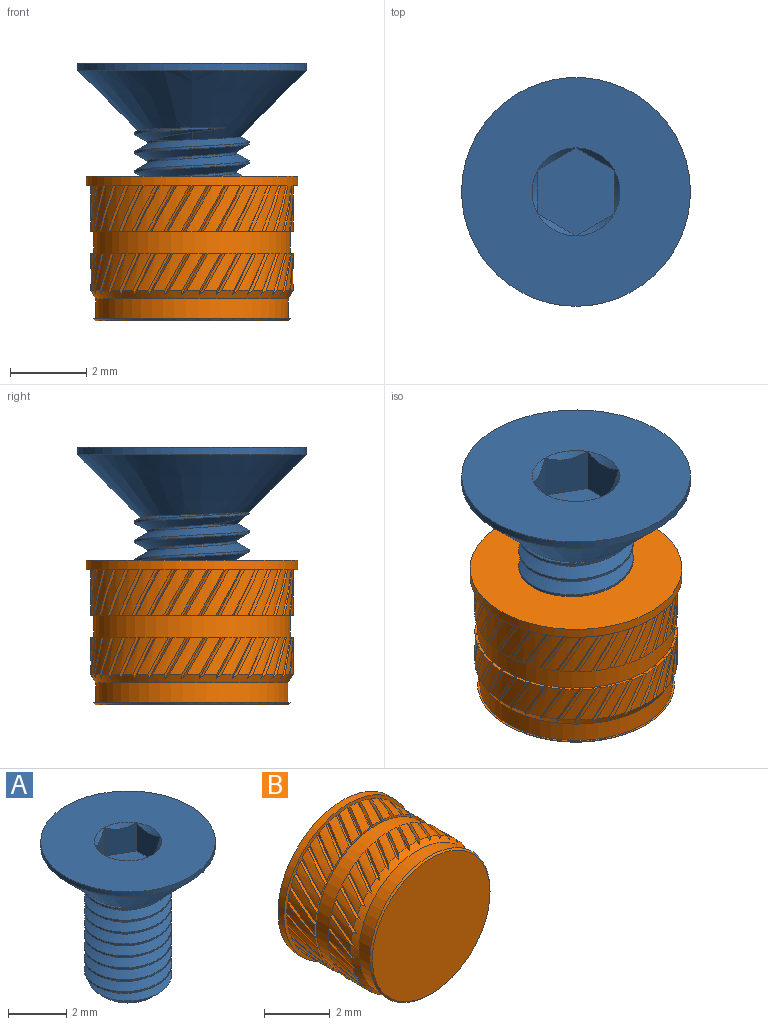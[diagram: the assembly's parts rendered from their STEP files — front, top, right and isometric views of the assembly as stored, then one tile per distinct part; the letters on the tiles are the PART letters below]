
ASSEMBLY  parts=2 mates=1
PART A: 23 faces, bbox 6.4x6.4x6.6 mm
  f0: cone r=1.15mm half-angle=45deg, axis (0,0,1), area 0.1mm2, adj f10,f17
  f1: cone r=1.5mm half-angle=45deg, axis (0,0,1), area 31.8mm2, adj f2,f3,f6,f7,f8
  f2: cone r=1.5mm half-angle=45deg, axis (0,0,1), area 0.2mm2, adj f1,f5,f7,f8
  f3: cylinder r=3mm len=6mm, axis (0,0,1), area 3.8mm2, adj f1,f10
  f4: cone r=1.12mm half-angle=45deg, axis (0,0,1), area 2.4mm2, adj f5,f6,f7,f8,f9
  f5: cylinder r=1.18mm len=3.93mm, axis (0,0,1), area 3.6mm2, adj f2,f4,f7,f8
  f6: cylinder r=1.5mm len=3.93mm, axis (0,0,-1), area 4.6mm2, adj f1,f4,f7,f8
  f7: bspline ~4.69x3.46mm, area 24.8mm2, adj f1,f2,f4,f5,f6
  f8: bspline ~4.35x3.46mm, area 24.8mm2, adj f1,f2,f4,f5,f6
  f9: plane 2.25x2.25mm, normal (0,0,-1), area 4mm2, adj f4
  f10: plane 6x6mm, normal (0,0,1), area 24.1mm2, adj f0,f3,f11,f12,f13,f14,f15
  f11: cone r=1.15mm half-angle=45deg, axis (0,0,1), area 0mm2, adj f10,f18
  f12: cone r=1.15mm half-angle=45deg, axis (0,0,1), area 0mm2, adj f10,f19
  f13: cone r=1.15mm half-angle=45deg, axis (0,0,1), area 0mm2, adj f10,f20
  f14: cone r=1.15mm half-angle=45deg, axis (0,0,1), area 0mm2, adj f10,f21
  f15: cone r=1.15mm half-angle=45deg, axis (0,0,1), area 0mm2, adj f10,f22
  f16: plane 2.31x2mm, normal (0,0,1), area 3.5mm2, adj f17,f18,f19,f20,f21,f22
  f17: plane 1.3x1.27mm, normal (-1,0,0), area 1.3mm2, adj f0,f16,f18,f22
  f18: plane 1.63x1.44mm, normal (-0.5,-0.87,0), area 1.3mm2, adj f11,f16,f17,f19
  f19: plane 1.63x1.44mm, normal (0.5,-0.87,0), area 1.3mm2, adj f12,f16,f18,f20
  f20: plane 1.63x1.59mm, normal (1,0,0), area 1.3mm2, adj f13,f16,f19,f21
  f21: plane 1.63x1.44mm, normal (0.5,0.87,0), area 1.3mm2, adj f14,f16,f20,f22
  f22: plane 1.63x1.44mm, normal (-0.5,0.87,0), area 1.3mm2, adj f15,f16,f17,f21
PART B: 227 faces, bbox 5.6x3.8x5.6 mm
  f0: cylinder r=2.58mm len=5.16mm, axis (0,1,0), area 9.3mm2, adj f225,f226
  f1: cone r=2.58mm half-angle=45deg, axis (0,1,0), area 1.2mm2, adj f151,f152
  f2: cone r=2.65mm half-angle=30deg, axis (0,1,0), area 3.9mm2, adj f5,f7,f8,f9,f10,f11,f12,f13
  f3: cylinder r=2.78mm len=5.56mm, axis (0,1,0), area 4.4mm2, adj f149,f150
  f4: cylinder r=2.65mm len=1.2mm, axis (0,1,0), area 0.4mm2, adj f149,f153,f156,f226
  f5: cylinder r=2.52mm len=5.05mm, axis (0,1,0), area 8.3mm2, adj f2,f151
  f6: cylinder r=2.65mm len=1.2mm, axis (0,1,0), area 0.4mm2, adj f149,f155,f158,f226
  f7: cylinder r=2.65mm len=0.97mm, axis (0,1,0), area 0.3mm2, adj f2,f47,f50,f225
  f8: cylinder r=2.65mm len=0.97mm, axis (0,1,0), area 0.3mm2, adj f2,f49,f51,f225
  f9: cylinder r=2.65mm len=0.97mm, axis (0,1,0), area 0.3mm2, adj f2,f111,f113,f225
  f10: cylinder r=2.65mm len=0.97mm, axis (0,1,0), area 0.3mm2, adj f2,f44,f114,f225
  f11: cylinder r=2.65mm len=0.97mm, axis (0,1,0), area 0.3mm2, adj f2,f109,f112,f225
  f12: cylinder r=2.65mm len=0.97mm, axis (0,1,0), area 0.3mm2, adj f2,f108,f110,f225
  f13: cylinder r=2.65mm len=0.97mm, axis (0,1,0), area 0.3mm2, adj f2,f103,f105,f225
  f14: cylinder r=2.65mm len=0.97mm, axis (0,1,0), area 0.3mm2, adj f2,f106,f107,f225
  f15: cylinder r=2.65mm len=0.97mm, axis (0,1,0), area 0.3mm2, adj f2,f101,f104,f225
  f16: cylinder r=2.65mm len=0.97mm, axis (0,1,0), area 0.3mm2, adj f2,f99,f102,f225
  f17: cylinder r=2.65mm len=0.97mm, axis (0,1,0), area 0.3mm2, adj f2,f97,f100,f225
  f18: cylinder r=2.65mm len=0.97mm, axis (0,1,0), area 0.3mm2, adj f2,f93,f95,f225
  f19: cylinder r=2.65mm len=0.97mm, axis (0,1,0), area 0.3mm2, adj f2,f96,f98,f225
  f20: cylinder r=2.65mm len=0.97mm, axis (0,1,0), area 0.3mm2, adj f2,f91,f94,f225
  f21: cylinder r=2.65mm len=0.97mm, axis (0,1,0), area 0.3mm2, adj f2,f90,f92,f225
  f22: cylinder r=2.65mm len=0.97mm, axis (0,1,0), area 0.3mm2, adj f2,f88,f89,f225
  f23: cylinder r=2.65mm len=0.97mm, axis (0,1,0), area 0.3mm2, adj f2,f85,f87,f225
  f24: cylinder r=2.65mm len=0.97mm, axis (0,1,0), area 0.3mm2, adj f2,f83,f86,f225
  f25: cylinder r=2.65mm len=0.97mm, axis (0,1,0), area 0.3mm2, adj f2,f81,f84,f225
  f26: cylinder r=2.65mm len=0.97mm, axis (0,1,0), area 0.3mm2, adj f2,f79,f82,f225
  f27: cylinder r=2.65mm len=0.97mm, axis (0,1,0), area 0.3mm2, adj f2,f78,f80,f225
  f28: cylinder r=2.65mm len=0.97mm, axis (0,1,0), area 0.3mm2, adj f2,f75,f77,f225
  f29: cylinder r=2.65mm len=0.97mm, axis (0,1,0), area 0.3mm2, adj f2,f73,f76,f225
  f30: cylinder r=2.65mm len=0.97mm, axis (0,1,0), area 0.3mm2, adj f2,f72,f74,f225
  f31: cylinder r=2.65mm len=0.97mm, axis (0,1,0), area 0.3mm2, adj f2,f67,f69,f225
  f32: cylinder r=2.65mm len=0.97mm, axis (0,1,0), area 0.3mm2, adj f2,f70,f71,f225
  f33: cylinder r=2.65mm len=0.97mm, axis (0,1,0), area 0.3mm2, adj f2,f65,f68,f225
  f34: cylinder r=2.65mm len=0.97mm, axis (0,1,0), area 0.3mm2, adj f2,f63,f66,f225
  f35: cylinder r=2.65mm len=0.97mm, axis (0,1,0), area 0.3mm2, adj f2,f61,f64,f225
  f36: cylinder r=2.65mm len=0.97mm, axis (0,1,0), area 0.3mm2, adj f2,f57,f59,f225
  f37: cylinder r=2.65mm len=0.97mm, axis (0,1,0), area 0.3mm2, adj f2,f60,f62,f225
  f38: cylinder r=2.65mm len=0.97mm, axis (0,1,0), area 0.3mm2, adj f2,f55,f58,f225
  f39: cylinder r=2.65mm len=0.97mm, axis (0,1,0), area 0.3mm2, adj f2,f52,f53,f225
  f40: cylinder r=2.65mm len=0.97mm, axis (0,1,0), area 0.3mm2, adj f2,f54,f56,f225
  f41: cylinder r=2.65mm len=0.97mm, axis (0,1,0), area 0.3mm2, adj f2,f45,f48,f225
  f42: cylinder r=2.65mm len=0.97mm, axis (0,1,0), area 0.3mm2, adj f2,f43,f46,f225
  f43: bspline ~1.08x0.57mm, area 0.1mm2, adj f2,f42,f44,f225
  f44: bspline ~1.21x0.69mm, area 0.1mm2, adj f2,f10,f43,f225
  f45: bspline ~1.08x0.63mm, area 0.1mm2, adj f2,f41,f46,f225
  f46: bspline ~1.21x0.74mm, area 0.1mm2, adj f2,f42,f45,f225
  f47: bspline ~1.08x0.67mm, area 0.1mm2, adj f2,f7,f48,f225
  f48: bspline ~1.21x0.76mm, area 0.1mm2, adj f2,f41,f47,f225
  f49: bspline ~1.08x0.69mm, area 0.1mm2, adj f2,f8,f50,f225
  f50: bspline ~1.21x0.76mm, area 0.1mm2, adj f2,f7,f49,f225
  f51: bspline ~1.31x0.79mm, area 0.1mm2, adj f2,f8,f52,f225
  f52: bspline ~1.31x0.81mm, area 0.1mm2, adj f2,f39,f51,f225
  f53: bspline ~1.31x0.74mm, area 0.1mm2, adj f2,f39,f54,f225
  f54: bspline ~1.31x0.78mm, area 0.1mm2, adj f2,f40,f53,f225
  f55: bspline ~1.21x0.67mm, area 0.1mm2, adj f2,f38,f56,f225
  f56: bspline ~1.21x0.62mm, area 0.1mm2, adj f2,f40,f55,f225
  f57: bspline ~1.21x0.6mm, area 0.1mm2, adj f2,f36,f58,f225
  f58: bspline ~1.21x0.54mm, area 0.1mm2, adj f2,f38,f57,f225
  f59: bspline ~1.31x0.67mm, area 0.1mm2, adj f2,f36,f60,f225
  f60: bspline ~1.31x0.6mm, area 0.1mm2, adj f2,f37,f59,f225
  f61: bspline ~1.08x0.57mm, area 0.1mm2, adj f2,f35,f62,f225
  f62: bspline ~1.21x0.69mm, area 0.1mm2, adj f2,f37,f61,f225
  f63: bspline ~1.08x0.63mm, area 0.1mm2, adj f2,f34,f64,f225
  f64: bspline ~1.21x0.74mm, area 0.1mm2, adj f2,f35,f63,f225
  f65: bspline ~1.08x0.67mm, area 0.1mm2, adj f2,f33,f66,f225
  f66: bspline ~1.21x0.76mm, area 0.1mm2, adj f2,f34,f65,f225
  f67: bspline ~1.08x0.69mm, area 0.1mm2, adj f2,f31,f68,f225
  f68: bspline ~1.21x0.76mm, area 0.1mm2, adj f2,f33,f67,f225
  f69: bspline ~1.31x0.79mm, area 0.1mm2, adj f2,f31,f70,f225
  f70: bspline ~1.31x0.81mm, area 0.1mm2, adj f2,f32,f69,f225
  f71: bspline ~1.31x0.74mm, area 0.1mm2, adj f2,f32,f72,f225
  f72: bspline ~1.31x0.78mm, area 0.1mm2, adj f2,f30,f71,f225
  f73: bspline ~1.21x0.67mm, area 0.1mm2, adj f2,f29,f74,f225
  f74: bspline ~1.21x0.62mm, area 0.1mm2, adj f2,f30,f73,f225
  f75: bspline ~1.21x0.6mm, area 0.1mm2, adj f2,f28,f76,f225
  f76: bspline ~1.21x0.54mm, area 0.1mm2, adj f2,f29,f75,f225
  f77: bspline ~1.31x0.67mm, area 0.1mm2, adj f2,f28,f78,f225
  f78: bspline ~1.31x0.6mm, area 0.1mm2, adj f2,f27,f77,f225
  f79: bspline ~1.08x0.57mm, area 0.1mm2, adj f2,f26,f80,f225
  f80: bspline ~1.21x0.69mm, area 0.1mm2, adj f2,f27,f79,f225
  f81: bspline ~1.08x0.63mm, area 0.1mm2, adj f2,f25,f82,f225
  f82: bspline ~1.21x0.74mm, area 0.1mm2, adj f2,f26,f81,f225
  f83: bspline ~1.08x0.67mm, area 0.1mm2, adj f2,f24,f84,f225
  f84: bspline ~1.21x0.76mm, area 0.1mm2, adj f2,f25,f83,f225
  f85: bspline ~1.08x0.69mm, area 0.1mm2, adj f2,f23,f86,f225
  f86: bspline ~1.21x0.76mm, area 0.1mm2, adj f2,f24,f85,f225
  f87: bspline ~1.31x0.79mm, area 0.1mm2, adj f2,f23,f88,f225
  f88: bspline ~1.31x0.81mm, area 0.1mm2, adj f2,f22,f87,f225
  f89: bspline ~1.31x0.74mm, area 0.1mm2, adj f2,f22,f90,f225
  f90: bspline ~1.31x0.78mm, area 0.1mm2, adj f2,f21,f89,f225
  f91: bspline ~1.21x0.67mm, area 0.1mm2, adj f2,f20,f92,f225
  f92: bspline ~1.21x0.62mm, area 0.1mm2, adj f2,f21,f91,f225
  f93: bspline ~1.21x0.6mm, area 0.1mm2, adj f2,f18,f94,f225
  f94: bspline ~1.21x0.54mm, area 0.1mm2, adj f2,f20,f93,f225
  f95: bspline ~1.31x0.67mm, area 0.1mm2, adj f2,f18,f96,f225
  f96: bspline ~1.31x0.6mm, area 0.1mm2, adj f2,f19,f95,f225
  f97: bspline ~1.08x0.57mm, area 0.1mm2, adj f2,f17,f98,f225
  f98: bspline ~1.21x0.69mm, area 0.1mm2, adj f2,f19,f97,f225
  f99: bspline ~1.08x0.63mm, area 0.1mm2, adj f2,f16,f100,f225
  f100: bspline ~1.21x0.74mm, area 0.1mm2, adj f2,f17,f99,f225
  f101: bspline ~1.08x0.67mm, area 0.1mm2, adj f2,f15,f102,f225
  f102: bspline ~1.21x0.76mm, area 0.1mm2, adj f2,f16,f101,f225
  f103: bspline ~1.08x0.69mm, area 0.1mm2, adj f2,f13,f104,f225
  f104: bspline ~1.21x0.76mm, area 0.1mm2, adj f2,f15,f103,f225
  f105: bspline ~1.31x0.79mm, area 0.1mm2, adj f2,f13,f106,f225
  f106: bspline ~1.31x0.81mm, area 0.1mm2, adj f2,f14,f105,f225
  f107: bspline ~1.31x0.74mm, area 0.1mm2, adj f2,f14,f108,f225
  f108: bspline ~1.31x0.78mm, area 0.1mm2, adj f2,f12,f107,f225
  f109: bspline ~1.21x0.67mm, area 0.1mm2, adj f2,f11,f110,f225
  f110: bspline ~1.21x0.62mm, area 0.1mm2, adj f2,f12,f109,f225
  f111: bspline ~1.21x0.6mm, area 0.1mm2, adj f2,f9,f112,f225
  f112: bspline ~1.21x0.54mm, area 0.1mm2, adj f2,f11,f111,f225
  f113: bspline ~1.31x0.67mm, area 0.1mm2, adj f2,f9,f114,f225
  f114: bspline ~1.31x0.6mm, area 0.1mm2, adj f2,f10,f113,f225
  f115: cylinder r=2.65mm len=1.2mm, axis (0,1,0), area 0.4mm2, adj f149,f221,f224,f226
  f116: cylinder r=2.65mm len=1.2mm, axis (0,1,0), area 0.4mm2, adj f149,f154,f223,f226
  f117: cylinder r=2.65mm len=1.2mm, axis (0,1,0), area 0.4mm2, adj f149,f219,f222,f226
  f118: cylinder r=2.65mm len=1.2mm, axis (0,1,0), area 0.4mm2, adj f149,f217,f220,f226
  f119: cylinder r=2.65mm len=1.2mm, axis (0,1,0), area 0.4mm2, adj f149,f213,f216,f226
  f120: cylinder r=2.65mm len=1.2mm, axis (0,1,0), area 0.4mm2, adj f149,f215,f218,f226
  f121: cylinder r=2.65mm len=1.2mm, axis (0,1,0), area 0.4mm2, adj f149,f211,f214,f226
  f122: cylinder r=2.65mm len=1.2mm, axis (0,1,0), area 0.4mm2, adj f149,f209,f212,f226
  f123: cylinder r=2.65mm len=1.2mm, axis (0,1,0), area 0.4mm2, adj f149,f207,f210,f226
  f124: cylinder r=2.65mm len=1.2mm, axis (0,1,0), area 0.4mm2, adj f149,f203,f206,f226
  f125: cylinder r=2.65mm len=1.2mm, axis (0,1,0), area 0.4mm2, adj f149,f205,f208,f226
  f126: cylinder r=2.65mm len=1.2mm, axis (0,1,0), area 0.4mm2, adj f149,f201,f204,f226
  f127: cylinder r=2.65mm len=1.2mm, axis (0,1,0), area 0.4mm2, adj f149,f199,f202,f226
  f128: cylinder r=2.65mm len=1.2mm, axis (0,1,0), area 0.4mm2, adj f149,f197,f200,f226
  f129: cylinder r=2.65mm len=1.2mm, axis (0,1,0), area 0.4mm2, adj f149,f195,f198,f226
  f130: cylinder r=2.65mm len=1.2mm, axis (0,1,0), area 0.4mm2, adj f149,f193,f196,f226
  f131: cylinder r=2.65mm len=1.2mm, axis (0,1,0), area 0.4mm2, adj f149,f191,f194,f226
  f132: cylinder r=2.65mm len=1.2mm, axis (0,1,0), area 0.4mm2, adj f149,f189,f192,f226
  f133: cylinder r=2.65mm len=1.2mm, axis (0,1,0), area 0.4mm2, adj f149,f187,f190,f226
  f134: cylinder r=2.65mm len=1.2mm, axis (0,1,0), area 0.4mm2, adj f149,f185,f188,f226
  f135: cylinder r=2.65mm len=1.2mm, axis (0,1,0), area 0.4mm2, adj f149,f183,f186,f226
  f136: cylinder r=2.65mm len=1.2mm, axis (0,1,0), area 0.4mm2, adj f149,f181,f184,f226
  f137: cylinder r=2.65mm len=1.2mm, axis (0,1,0), area 0.4mm2, adj f149,f177,f180,f226
  f138: cylinder r=2.65mm len=1.2mm, axis (0,1,0), area 0.4mm2, adj f149,f179,f182,f226
  f139: cylinder r=2.65mm len=1.2mm, axis (0,1,0), area 0.4mm2, adj f149,f175,f178,f226
  f140: cylinder r=2.65mm len=1.2mm, axis (0,1,0), area 0.4mm2, adj f149,f173,f176,f226
  f141: cylinder r=2.65mm len=1.2mm, axis (0,1,0), area 0.4mm2, adj f149,f171,f174,f226
  f142: cylinder r=2.65mm len=1.2mm, axis (0,1,0), area 0.4mm2, adj f149,f167,f170,f226
  f143: cylinder r=2.65mm len=1.2mm, axis (0,1,0), area 0.4mm2, adj f149,f169,f172,f226
  f144: cylinder r=2.65mm len=1.2mm, axis (0,1,0), area 0.4mm2, adj f149,f165,f168,f226
  f145: cylinder r=2.65mm len=1.2mm, axis (0,1,0), area 0.4mm2, adj f149,f161,f164,f226
  f146: cylinder r=2.65mm len=1.2mm, axis (0,1,0), area 0.4mm2, adj f149,f163,f166,f226
  f147: cylinder r=2.65mm len=1.2mm, axis (0,1,0), area 0.4mm2, adj f149,f159,f162,f226
  f148: cylinder r=2.65mm len=1.2mm, axis (0,1,0), area 0.4mm2, adj f149,f157,f160,f226
  f149: plane 5.56x5.56mm, normal (0,-1,0), area 2.3mm2, adj f3,f4,f6,f115,f116,f117,f118,f119
  f150: plane 5.56x5.56mm, normal (0,1,0), area 24.3mm2, adj f3
  f151: plane 5.16x5.16mm, normal (0,1,0), area 0.9mm2, adj f1,f5
  f152: plane 5.05x5.05mm, normal (0,-1,0), area 20mm2, adj f1
  f153: bspline ~1.31x0.79mm, area 0.1mm2, adj f4,f149,f154,f226
  f154: bspline ~1.31x0.81mm, area 0.1mm2, adj f116,f149,f153,f226
  f155: bspline ~1.31x0.81mm, area 0.1mm2, adj f6,f149,f156,f226
  f156: bspline ~1.31x0.81mm, area 0.1mm2, adj f4,f149,f155,f226
  f157: bspline ~1.31x0.81mm, area 0.1mm2, adj f148,f149,f158,f226
  f158: bspline ~1.31x0.78mm, area 0.1mm2, adj f6,f149,f157,f226
  f159: bspline ~1.2x0.71mm, area 0.1mm2, adj f147,f149,f160,f226
  f160: bspline ~1.31x0.73mm, area 0.1mm2, adj f148,f149,f159,f226
  f161: bspline ~1.31x0.72mm, area 0.1mm2, adj f145,f149,f162,f226
  f162: bspline ~1.31x0.66mm, area 0.1mm2, adj f147,f149,f161,f226
  f163: bspline ~1.31x0.64mm, area 0.1mm2, adj f146,f149,f164,f226
  f164: bspline ~1.31x0.58mm, area 0.1mm2, adj f145,f149,f163,f226
  f165: bspline ~1.2x0.56mm, area 0.1mm2, adj f144,f149,f166,f226
  f166: bspline ~1.31x0.67mm, area 0.1mm2, adj f146,f149,f165,f226
  f167: bspline ~1.2x0.64mm, area 0.1mm2, adj f142,f149,f168,f226
  f168: bspline ~1.31x0.74mm, area 0.1mm2, adj f144,f149,f167,f226
  f169: bspline ~1.31x0.75mm, area 0.1mm2, adj f143,f149,f170,f226
  f170: bspline ~1.31x0.79mm, area 0.1mm2, adj f142,f149,f169,f226
  f171: bspline ~1.31x0.79mm, area 0.1mm2, adj f141,f149,f172,f226
  f172: bspline ~1.31x0.81mm, area 0.1mm2, adj f143,f149,f171,f226
  f173: bspline ~1.31x0.81mm, area 0.1mm2, adj f140,f149,f174,f226
  f174: bspline ~1.31x0.81mm, area 0.1mm2, adj f141,f149,f173,f226
  f175: bspline ~1.31x0.81mm, area 0.1mm2, adj f139,f149,f176,f226
  f176: bspline ~1.31x0.78mm, area 0.1mm2, adj f140,f149,f175,f226
  f177: bspline ~1.2x0.71mm, area 0.1mm2, adj f137,f149,f178,f226
  f178: bspline ~1.31x0.73mm, area 0.1mm2, adj f139,f149,f177,f226
  f179: bspline ~1.31x0.72mm, area 0.1mm2, adj f138,f149,f180,f226
  f180: bspline ~1.31x0.66mm, area 0.1mm2, adj f137,f149,f179,f226
  f181: bspline ~1.31x0.64mm, area 0.1mm2, adj f136,f149,f182,f226
  f182: bspline ~1.31x0.58mm, area 0.1mm2, adj f138,f149,f181,f226
  f183: bspline ~1.2x0.56mm, area 0.1mm2, adj f135,f149,f184,f226
  f184: bspline ~1.31x0.67mm, area 0.1mm2, adj f136,f149,f183,f226
  f185: bspline ~1.2x0.64mm, area 0.1mm2, adj f134,f149,f186,f226
  f186: bspline ~1.31x0.74mm, area 0.1mm2, adj f135,f149,f185,f226
  f187: bspline ~1.31x0.75mm, area 0.1mm2, adj f133,f149,f188,f226
  f188: bspline ~1.31x0.79mm, area 0.1mm2, adj f134,f149,f187,f226
  f189: bspline ~1.31x0.79mm, area 0.1mm2, adj f132,f149,f190,f226
  f190: bspline ~1.31x0.81mm, area 0.1mm2, adj f133,f149,f189,f226
  f191: bspline ~1.31x0.81mm, area 0.1mm2, adj f131,f149,f192,f226
  f192: bspline ~1.31x0.81mm, area 0.1mm2, adj f132,f149,f191,f226
  f193: bspline ~1.31x0.81mm, area 0.1mm2, adj f130,f149,f194,f226
  f194: bspline ~1.31x0.78mm, area 0.1mm2, adj f131,f149,f193,f226
  f195: bspline ~1.2x0.71mm, area 0.1mm2, adj f129,f149,f196,f226
  f196: bspline ~1.31x0.73mm, area 0.1mm2, adj f130,f149,f195,f226
  f197: bspline ~1.31x0.72mm, area 0.1mm2, adj f128,f149,f198,f226
  f198: bspline ~1.31x0.66mm, area 0.1mm2, adj f129,f149,f197,f226
  f199: bspline ~1.31x0.64mm, area 0.1mm2, adj f127,f149,f200,f226
  f200: bspline ~1.31x0.58mm, area 0.1mm2, adj f128,f149,f199,f226
  f201: bspline ~1.2x0.56mm, area 0.1mm2, adj f126,f149,f202,f226
  f202: bspline ~1.31x0.67mm, area 0.1mm2, adj f127,f149,f201,f226
  f203: bspline ~1.2x0.64mm, area 0.1mm2, adj f124,f149,f204,f226
  f204: bspline ~1.31x0.74mm, area 0.1mm2, adj f126,f149,f203,f226
  f205: bspline ~1.31x0.75mm, area 0.1mm2, adj f125,f149,f206,f226
  f206: bspline ~1.31x0.79mm, area 0.1mm2, adj f124,f149,f205,f226
  f207: bspline ~1.31x0.79mm, area 0.1mm2, adj f123,f149,f208,f226
  f208: bspline ~1.31x0.81mm, area 0.1mm2, adj f125,f149,f207,f226
  f209: bspline ~1.31x0.81mm, area 0.1mm2, adj f122,f149,f210,f226
  f210: bspline ~1.31x0.81mm, area 0.1mm2, adj f123,f149,f209,f226
  f211: bspline ~1.31x0.81mm, area 0.1mm2, adj f121,f149,f212,f226
  f212: bspline ~1.31x0.78mm, area 0.1mm2, adj f122,f149,f211,f226
  f213: bspline ~1.2x0.71mm, area 0.1mm2, adj f119,f149,f214,f226
  f214: bspline ~1.31x0.73mm, area 0.1mm2, adj f121,f149,f213,f226
  f215: bspline ~1.31x0.72mm, area 0.1mm2, adj f120,f149,f216,f226
  f216: bspline ~1.31x0.66mm, area 0.1mm2, adj f119,f149,f215,f226
  f217: bspline ~1.31x0.64mm, area 0.1mm2, adj f118,f149,f218,f226
  f218: bspline ~1.31x0.58mm, area 0.1mm2, adj f120,f149,f217,f226
  f219: bspline ~1.2x0.56mm, area 0.1mm2, adj f117,f149,f220,f226
  f220: bspline ~1.31x0.67mm, area 0.1mm2, adj f118,f149,f219,f226
  f221: bspline ~1.2x0.64mm, area 0.1mm2, adj f115,f149,f222,f226
  f222: bspline ~1.31x0.74mm, area 0.1mm2, adj f117,f149,f221,f226
  f223: bspline ~1.31x0.75mm, area 0.1mm2, adj f116,f149,f224,f226
  f224: bspline ~1.31x0.79mm, area 0.1mm2, adj f115,f149,f223,f226
  f225: plane 5.31x5.31mm, normal (0,1,0), area 1.1mm2, adj f0,f7,f8,f9,f10,f11,f12,f13
  f226: plane 5.31x5.31mm, normal (0,-1,0), area 1.1mm2, adj f0,f4,f6,f115,f116,f117,f118,f119
PLACE A at identity fixed
PLACE B rot(axis=(1,0,0),90deg) t=(0,0,-2.96)mm
MATE fastened B.f2 <-> A.f3  axis (0,0,-1) through (0,0,-6.76)mm
